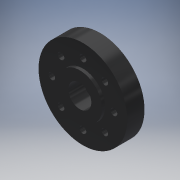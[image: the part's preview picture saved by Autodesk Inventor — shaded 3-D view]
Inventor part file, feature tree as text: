
AUTODESK INVENTOR PART (.ipt)
format: ipt  version: 2018 (Build 220112000, 112)  size: 154,624 bytes
history: native  units: in
note: dims shown in document units (in); Inventor stores cm internally (conversion verified against a paired STEP export)
features: extrude x1, sketch x1, projected_geometry x1, other x1
ambient origin geometry x8: Origin, YZ Plane, XZ Plane, XY Plane, X Axis, Y Axis, Z Axis, Center Point
bodies: Solid1 (feature_tree)
feature tree (4):
  extrude  "Extrusion1"  [1 undecoded]
  sketch  "Sketch1"  dims[d0=0.0276in d1=0.0in]
  projected_geometry  "Projected Loop1"
  other  "ÊäÈë1"
note: 1 required parameter value undecoded (feature->parameter linkage not recoverable at this tier; creation-order binding heuristic only, values carry confidence <= 0.55)
